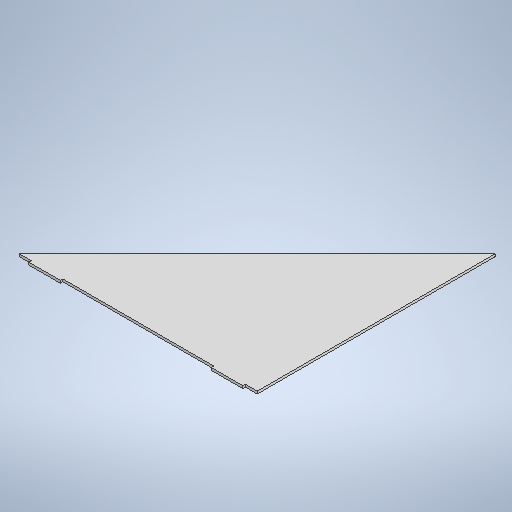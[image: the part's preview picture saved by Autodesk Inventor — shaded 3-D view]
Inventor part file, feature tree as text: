
AUTODESK INVENTOR PART (.ipt)
format: ipt  version: 2025.2 (Build 292293000, 293)  size: 245,760 bytes
history: native  units: mm
features: extrude x1, sketch x1
ambient origin geometry x8: Origin, YZ Plane, XZ Plane, XY Plane, X Axis, Y Axis, Z Axis, Center Point
bodies: Solid1 (feature_tree)
feature tree (2):
  extrude  "Extrusion1"  TaperAngle=45.0deg  [1 undecoded]
  sketch  "Sketch1"  dims[d0=301.4mm d1=45.0deg d2=15.0mm d3=3.2mm d4=40.0mm d5=15.0mm d6=40.0mm d7=3.175mm d8=0.0mm d9=0.5mm d10=0.872665mm]
note: 1 required parameter value undecoded (feature->parameter linkage not recoverable at this tier; creation-order binding heuristic only, values carry confidence <= 0.55)
